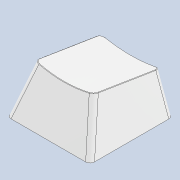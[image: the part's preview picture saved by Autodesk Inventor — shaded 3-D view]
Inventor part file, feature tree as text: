
AUTODESK INVENTOR PART (.ipt)
format: ipt  version: 2021 (Build 250183000, 183)  size: 251,392 bytes
history: native  units: in
note: dims shown in document units (in); Inventor stores cm internally (conversion verified against a paired STEP export)
features: chamfer x1
ambient origin geometry x8: Origin, YZ Plane, XZ Plane, XY Plane, X Axis, Y Axis, Z Axis, Center Point
bodies: Solid1 (feature_tree)
feature tree (1):
  chamfer  "Chamfer1"  [1 undecoded]
note: 1 required parameter value undecoded (feature->parameter linkage not recoverable at this tier; creation-order binding heuristic only, values carry confidence <= 0.55)
